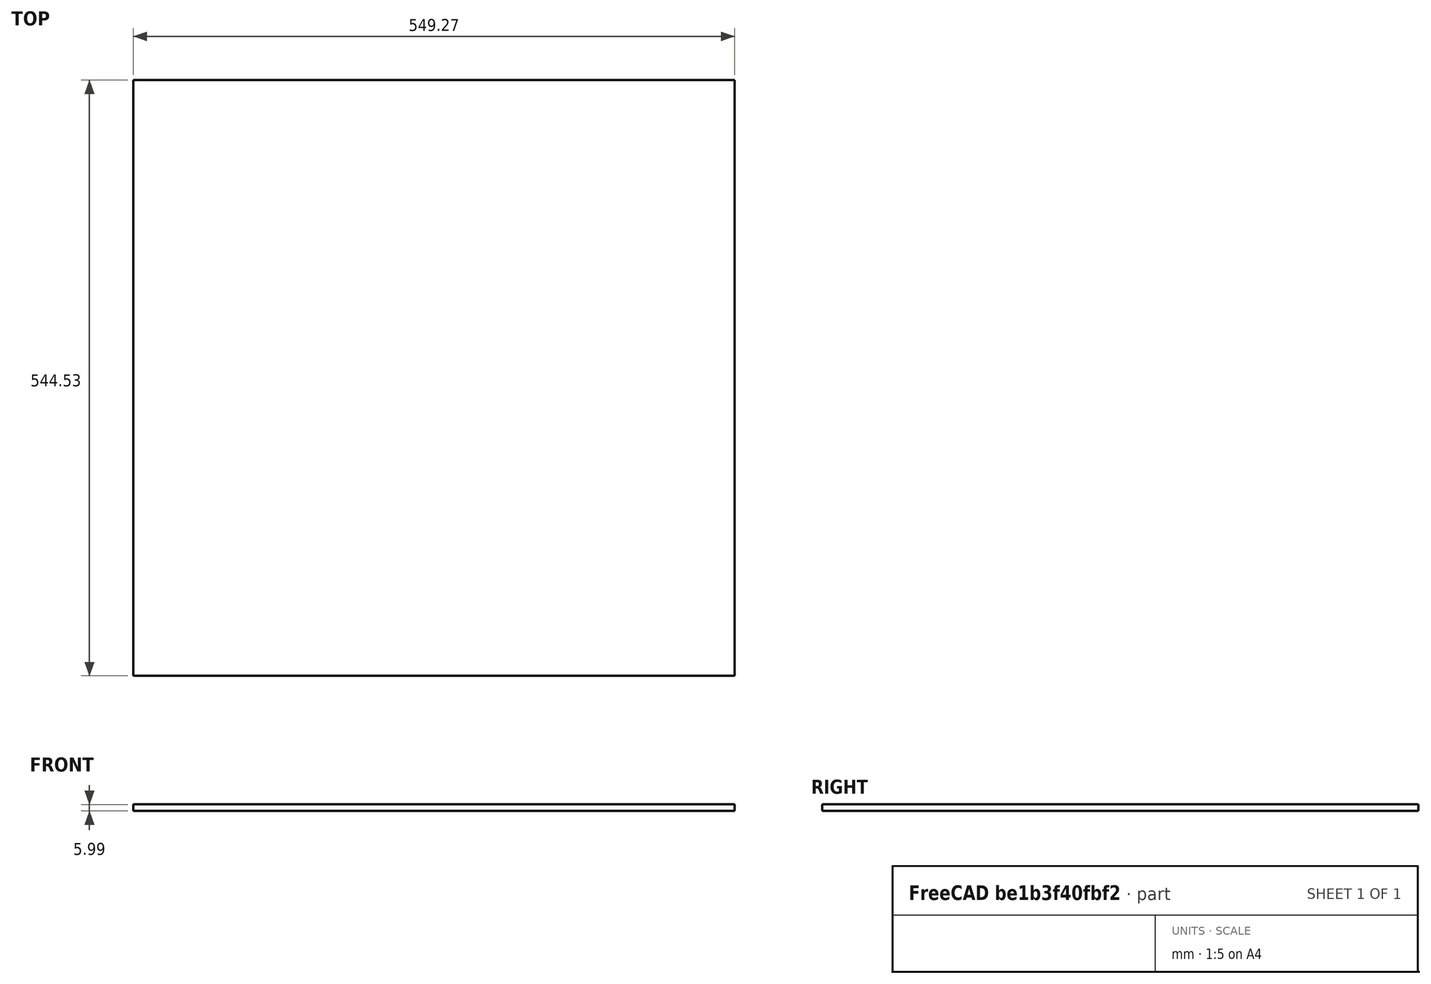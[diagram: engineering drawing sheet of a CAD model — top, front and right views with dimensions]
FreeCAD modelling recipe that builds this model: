
FCSTD DOCUMENT  (FreeCAD 0.19R24267 (Git))
Label: Inv2-P3
License: All rights reserved
LicenseURL: http://en.wikipedia.org/wiki/All_rights_reserved
objects: TechDraw::DrawViewDimension×3, TechDraw::DrawProjGroupItem×2, TechDraw::DrawHatch×2, TechDraw::DrawViewAnnotation×2, Sketcher::SketchObject×1, Part::Extrusion×1, TechDraw::DrawSVGTemplate×1, TechDraw::DrawProjGroup×1, TechDraw::DrawPage×1
note: 2 computed .brp shape members not serialized (recipe doc carries the construction recipe); baked Part::Feature solids carry a one-line shape summary decoded from their .brp

FEATURE [Sketcher::SketchObject] Sketch
  FullyConstrained = false
  sketch-geometry (4):
    g0: LineSegment StartX=-262.661 StartY=259.399 StartZ=0 EndX=286.614 EndY=259.399 EndZ=0
    g1: LineSegment StartX=286.614 StartY=259.399 StartZ=0 EndX=286.614 EndY=-285.126 EndZ=0
    g2: LineSegment StartX=286.614 StartY=-285.126 StartZ=0 EndX=-262.661 EndY=-285.126 EndZ=0
    g3: LineSegment StartX=-262.661 StartY=-285.126 StartZ=0 EndX=-262.661 EndY=259.399 EndZ=0
  constraints (10):
    c: Coincident(g0,g1)
    c: Coincident(g1,g2)
    c: Coincident(g2,g3)
    c: Coincident(g3,g0)
    c: Horizontal(g0)
    c: Horizontal(g2)
    c: Vertical(g1)
    c: Vertical(g3)
    c: DistanceX(g2,g2) = 549.275
    c: DistanceY(g3,g3) = 544.525
FEATURE [Part::Extrusion] Extrude
  Base = -> Sketch
  Dir = (0,0,1)
  DirMode = 2
  FaceMakerClass = Part::FaceMakerBullseye
  LengthFwd = 5.9944
  LengthRev = 0
  Solid = true
  Symmetric = false
FEATURE [TechDraw::DrawSVGTemplate] Template
  Height = 215.9
  Orientation = 1
  Width = 279.4
FEATURE [TechDraw::DrawProjGroupItem] ProjItem  label="Front"
  CoarseView = false
  Direction = (0,0,1)
  Focus = 100
  HardHidden = false
  IsoCount = 0
  IsoHidden = false
  IsoVisible = false
  LockPosition = true
  Perspective = false
  Rotation = 0
  RotationVector = (-1,0,0)
  Scale = 0.2
  ScaleType = 2
  SeamHidden = false
  SeamVisible = true
  SmoothHidden = false
  SmoothVisible = true
  Source = -> [Extrude]
  Type = 0
  X = 0
  XDirection = (-1,0,0)
  Y = 0
FEATURE [TechDraw::DrawProjGroupItem] ProjItem001  label="Left"
  CoarseView = false
  Direction = (1,0,1e-16)
  Focus = 100
  HardHidden = false
  IsoCount = 0
  IsoHidden = false
  IsoVisible = false
  LockPosition = false
  Perspective = false
  Rotation = 0
  RotationVector = (1,0,0)
  Scale = 0.2
  ScaleType = 2
  SeamHidden = false
  SeamVisible = true
  SmoothHidden = false
  SmoothVisible = true
  Source = -> [Extrude]
  Type = 1
  X = 85.1166
  XDirection = (-1e-16,0,1)
  Y = 0
FEATURE [TechDraw::DrawProjGroup] ProjGroup
  Anchor = -> ProjItem
  AutoDistribute = true
  LockPosition = false
  ProjectionType = 0
  Rotation = 0
  Scale = 0.2
  ScaleType = 2
  Source = -> [Extrude]
  Views = -> [ProjItem,ProjItem001]
  X = 129.946
  Y = 108.623
  spacingX = 15.0114
  spacingY = 15.0114
FEATURE [TechDraw::DrawHatch] Hatch  label="HatchF0"
  HatchPattern = <path>
  Source = -> ProjItem [Face0]
FEATURE [TechDraw::DrawHatch] Hatch001  label="Hatch001F0"
  HatchPattern = <path>
  Source = -> ProjItem001 [Face0]
FEATURE [TechDraw::DrawViewDimension] Dimension
  Arbitrary = false
  ArbitraryTolerances = false
  EqualTolerance = true
  FormatSpec = %.3f
  FormatSpecOverTolerance = %+.3f
  FormatSpecUnderTolerance = %+.3f
  Inverted = false
  LockPosition = false
  MeasureType = 1
  OverTolerance = 0
  References2D = -> [ProjItem]
  Rotation = 0
  ScaleType = 0
  TheoreticalExact = false
  Type = 2
  UnderTolerance = 0
  X = 60.0659
  Y = -0.233562
FEATURE [TechDraw::DrawViewDimension] Dimension001
  Arbitrary = false
  ArbitraryTolerances = false
  EqualTolerance = true
  FormatSpec = %.3f
  FormatSpecOverTolerance = %+.3f
  FormatSpecUnderTolerance = %+.3f
  Inverted = false
  LockPosition = false
  MeasureType = 1
  OverTolerance = 0
  References2D = -> [ProjItem]
  Rotation = 0
  ScaleType = 0
  TheoreticalExact = false
  Type = 1
  UnderTolerance = 0
  X = -0.700686
  Y = -59.8244
FEATURE [TechDraw::DrawViewDimension] Dimension002
  Arbitrary = false
  ArbitraryTolerances = false
  EqualTolerance = true
  FormatSpec = %.3f
  FormatSpecOverTolerance = %+.3f
  FormatSpecUnderTolerance = %+.3f
  Inverted = false
  LockPosition = false
  MeasureType = 1
  OverTolerance = 0
  References2D = -> [ProjItem001]
  Rotation = 0
  ScaleType = 0
  TheoreticalExact = false
  Type = 1
  UnderTolerance = 0
  X = 17.9279
  Y = 44.503
FEATURE [TechDraw::DrawViewAnnotation] Annotation
  Font = osifont
  LineSpace = 80
  LockPosition = false
  MaxWidth = -1
  Rotation = 0
  ScaleType = 0
  Text = Figure S2 (Inverted 2) | Panel 3 [back upper] | Quantity: 1
  TextSize = 5.0038
  TextStyle = 0
  X = 32.4753
  Y = 195.58
FEATURE [TechDraw::DrawViewAnnotation] Annotation002
  Font = osifont
  LineSpace = 80
  LockPosition = false
  MaxWidth = -1
  Rotation = 0
  ScaleType = 0
  Text = Units: Inches
  TextSize = 5.0038
  TextStyle = 0
  X = 259.08
  Y = 5.08
FEATURE [TechDraw::DrawPage] Page
  KeepUpdated = true
  NextBalloonIndex = 1
  ProjectionType = 0
  Template = -> Template
  Views = -> [ProjGroup,Dimension,Dimension001,Dimension002,Annotation,Annotation002]
note: 2 file-system paths scrubbed to <path> (originals preserved in the JSON sidecar)
